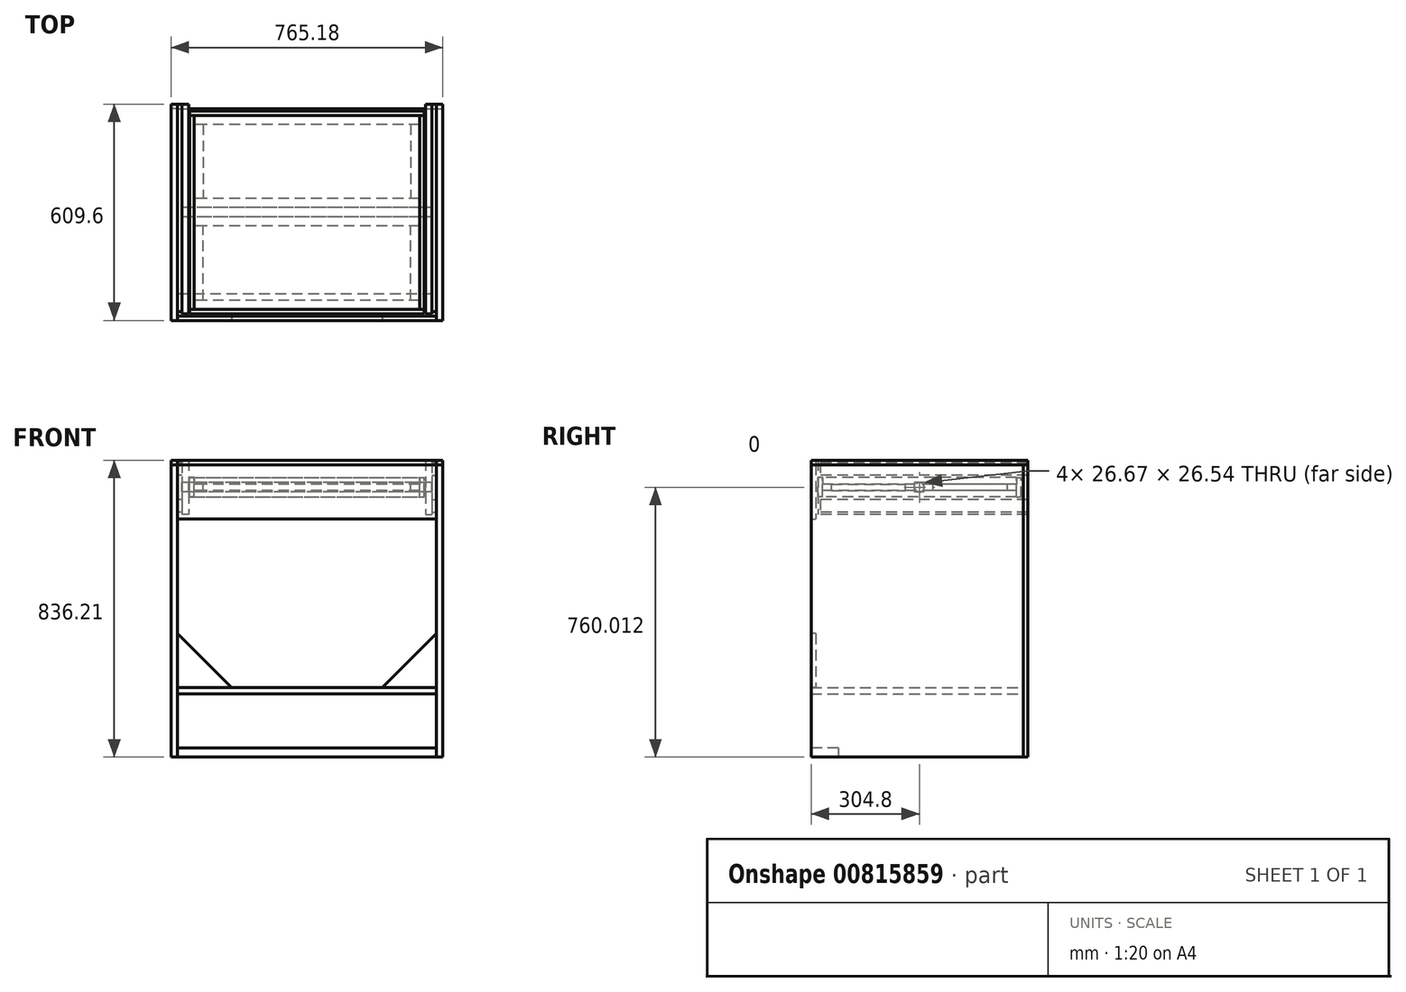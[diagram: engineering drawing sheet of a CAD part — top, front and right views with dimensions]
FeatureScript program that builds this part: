
annotation { "Feature Type Name" : "Feature", "Feature Type Description" : "" }
export const myFeature = defineFeature(function(context is Context, id is Id, definition is map)
    precondition{}
    {
        {
            var Q0;
            Q0=qCreatedBy(makeId("Top.planeOp"),FACE);
            var sketch = newSketch(context, id + "F0", { "sketchPlane" : qUnion([Q0])});
            skLineSegment(sketch, "E0.bottom", {"start": v(-317.5, 241.3) * mm, "end": v(317.5, 241.3) * mm});
            skLineSegment(sketch, "E0.top", {"start": v(-317.5, -304.8) * mm, "end": v(317.5, -304.8) * mm});
            skLineSegment(sketch, "E0.left", {"start": v(-317.5, 241.3) * mm, "end": v(-317.5, -304.8) * mm});
            skLineSegment(sketch, "E0.right", {"start": v(317.5, 241.3) * mm, "end": v(317.5, -304.8) * mm});
            skLineSegment(sketch, "E1", {"start": v(317.5, -18.41) * mm, "end": v(-317.5, -18.42) * mm});
            skLineSegment(sketch, "E2", {"start": v(317.5, -31.75) * mm, "end": v(-317.5, -31.75) * mm, "construction": true});
            skLineSegment(sketch, "E3", {"start": v(317.5, 6.99) * mm, "end": v(-317.5, 6.98) * mm});
            skLineSegment(sketch, "E4", {"start": v(317.5, 215.9) * mm, "end": v(-317.5, 215.9) * mm});
            skLineSegment(sketch, "E5", {"start": v(292.1, 215.9) * mm, "end": v(292.1, 6.98) * mm});
            skLineSegment(sketch, "E6", {"start": v(0, 0) * mm, "end": v(0, -123.63) * mm, "construction": true});
            skLineSegment(sketch, "E7.MirrorCS", {"start": v(-292.1, 215.9) * mm, "end": v(-292.1, 6.98) * mm});
            skLineSegment(sketch, "E8.MirrorCS", {"start": v(317.5, -45.08) * mm, "end": v(-317.5, -45.09) * mm});
            skLineSegment(sketch, "E9.MirrorCS", {"start": v(317.5, -70.48) * mm, "end": v(-317.5, -70.49) * mm});
            skLineSegment(sketch, "E10.MirrorCS", {"start": v(292.1, -279.4) * mm, "end": v(292.1, -70.49) * mm});
            skLineSegment(sketch, "E11.MirrorCS", {"start": v(317.5, -279.4) * mm, "end": v(-317.5, -279.4) * mm});
            skLineSegment(sketch, "E12.MirrorCS", {"start": v(-292.1, -279.4) * mm, "end": v(-292.1, -70.49) * mm});
            skSolve(sketch);
        }
        {
            var Q0;
            {var subQ1=sQuery(id+"F0.wireOp",EDGE,"E0.bottom");Q0=makeQuery(id+"F0.imprint","IMPRINT",FACE,{"disambiguationData":[TD([[makeQuery(id+"F0.imprint","IMPRINT",EDGE,{"derivedFrom":subQ1}),-1.0]])]});}
            var Q1;
            {var subQ0=sQuery(id+"F0.wireOp",EDGE,"E5");Q1=makeQuery(id+"F0.imprint","IMPRINT",FACE,{"disambiguationData":[TD([[makeQuery(id+"F0.imprint","IMPRINT",EDGE,{"derivedFrom":subQ0}),-1.0]])]});}
            var Q2;
            {var subQ5=sQuery(id+"F0.wireOp",EDGE,"E7.MirrorCS");Q2=makeQuery(id+"F0.imprint","IMPRINT",FACE,{"disambiguationData":[TD([[makeQuery(id+"F0.imprint","IMPRINT",EDGE,{"derivedFrom":subQ5}),-1.0]])]});}
            var Q3;
            {var subQ5=sQuery(id+"F0.wireOp",EDGE,"E5");Q3=makeQuery(id+"F0.imprint","IMPRINT",FACE,{"disambiguationData":[TD([[makeQuery(id+"F0.imprint","IMPRINT",EDGE,{"derivedFrom":subQ5}),1.0]])]});}
            var Q4;
            {var subQ4=sQuery(id+"F0.wireOp",EDGE,"E1");Q4=makeQuery(id+"F0.imprint","IMPRINT",FACE,{"disambiguationData":[TD([[makeQuery(id+"F0.imprint","IMPRINT",EDGE,{"derivedFrom":subQ4}),-1.0]])]});}
            var Q5;
            {var subQ0=sQuery(id+"F0.wireOp",EDGE,"E1");Q5=makeQuery(id+"F0.imprint","IMPRINT",FACE,{"disambiguationData":[TD([[makeQuery(id+"F0.imprint","IMPRINT",EDGE,{"derivedFrom":subQ0}),1.0]])]});}
            var Q6;
            {var subQ0=sQuery(id+"F0.wireOp",EDGE,"E8.MirrorCS");Q6=makeQuery(id+"F0.imprint","IMPRINT",FACE,{"disambiguationData":[TD([[makeQuery(id+"F0.imprint","IMPRINT",EDGE,{"derivedFrom":subQ0}),1.0]])]});}
            var Q7;
            {var subQ5=sQuery(id+"F0.wireOp",EDGE,"E10.MirrorCS");Q7=makeQuery(id+"F0.imprint","IMPRINT",FACE,{"disambiguationData":[TD([[makeQuery(id+"F0.imprint","IMPRINT",EDGE,{"derivedFrom":subQ5}),-1.0]])]});}
            var Q8;
            {var subQ0=sQuery(id+"F0.wireOp",EDGE,"E10.MirrorCS");Q8=makeQuery(id+"F0.imprint","IMPRINT",FACE,{"disambiguationData":[TD([[makeQuery(id+"F0.imprint","IMPRINT",EDGE,{"derivedFrom":subQ0}),1.0]])]});}
            var Q9;
            {var subQ5=sQuery(id+"F0.wireOp",EDGE,"E0.top");Q9=makeQuery(id+"F0.imprint","IMPRINT",FACE,{"disambiguationData":[TD([[makeQuery(id+"F0.imprint","IMPRINT",EDGE,{"derivedFrom":subQ5}),1.0]])]});}
            var Q10;
            {var subQ5=sQuery(id+"F0.wireOp",EDGE,"E12.MirrorCS");Q10=makeQuery(id+"F0.imprint","IMPRINT",FACE,{"disambiguationData":[TD([[makeQuery(id+"F0.imprint","IMPRINT",EDGE,{"derivedFrom":subQ5}),1.0]])]});}
            extrude(context, id + "F1", {"entities" : qUnion([Q0, Q1, Q2, Q3, Q4, Q5, Q6, Q7, Q8, Q9, Q10]), "depth" : 18.26 * mm, "offsetDistance" : 25.4 * mm});
        }
        {
            var Q0;
            {var subQ0=sQuery(id+"F0.wireOp",EDGE,"E1");Q0=makeQuery(id+"F0.imprint","IMPRINT",FACE,{"disambiguationData":[TD([[makeQuery(id+"F0.imprint","IMPRINT",EDGE,{"derivedFrom":subQ0}),1.0]])]});}
            extrude(context, id + "F2", {"entities" : qUnion([Q0]), "operationType" : NewBodyOperationType.REMOVE, "depth" : 4.14 * mm, "offsetDistance" : 25.4 * mm});
        }
        {
            var Q0;
            {var subQ0=sQuery(id+"F0.wireOp",EDGE,"E8.MirrorCS");Q0=makeQuery(id+"F0.imprint","IMPRINT",FACE,{"disambiguationData":[TD([[makeQuery(id+"F0.imprint","IMPRINT",EDGE,{"derivedFrom":subQ0}),1.0]])]});}
            var Q1;
            {var subQ4=sQuery(id+"F0.wireOp",EDGE,"E1");Q1=makeQuery(id+"F0.imprint","IMPRINT",FACE,{"disambiguationData":[TD([[makeQuery(id+"F0.imprint","IMPRINT",EDGE,{"derivedFrom":subQ4}),-1.0]])]});}
            var Q2;
            {var subQ1=sQuery(id+"F0.wireOp",EDGE,"E0.bottom");Q2=makeQuery(id+"F0.imprint","IMPRINT",FACE,{"disambiguationData":[TD([[makeQuery(id+"F0.imprint","IMPRINT",EDGE,{"derivedFrom":subQ1}),-1.0]])]});}
            var Q3;
            {var subQ5=sQuery(id+"F0.wireOp",EDGE,"E0.top");Q3=makeQuery(id+"F0.imprint","IMPRINT",FACE,{"disambiguationData":[TD([[makeQuery(id+"F0.imprint","IMPRINT",EDGE,{"derivedFrom":subQ5}),1.0]])]});}
            extrude(context, id + "F3", {"entities" : qUnion([Q0, Q1, Q2, Q3]), "oppositeDirection" : true, "depth" : 18.26 * mm, "offsetDistance" : 25.4 * mm});
        }
        {
            var Q0;
            {var subQ5=sQuery(id+"F0.wireOp",EDGE,"E10.MirrorCS");Q0=makeQuery(id+"F0.imprint","IMPRINT",FACE,{"disambiguationData":[TD([[makeQuery(id+"F0.imprint","IMPRINT",EDGE,{"derivedFrom":subQ5}),-1.0]])]});}
            var Q1;
            {var subQ5=sQuery(id+"F0.wireOp",EDGE,"E5");Q1=makeQuery(id+"F0.imprint","IMPRINT",FACE,{"disambiguationData":[TD([[makeQuery(id+"F0.imprint","IMPRINT",EDGE,{"derivedFrom":subQ5}),1.0]])]});}
            var Q2;
            {var subQ5=sQuery(id+"F0.wireOp",EDGE,"E7.MirrorCS");Q2=makeQuery(id+"F0.imprint","IMPRINT",FACE,{"disambiguationData":[TD([[makeQuery(id+"F0.imprint","IMPRINT",EDGE,{"derivedFrom":subQ5}),-1.0]])]});}
            var Q3;
            {var subQ5=sQuery(id+"F0.wireOp",EDGE,"E12.MirrorCS");Q3=makeQuery(id+"F0.imprint","IMPRINT",FACE,{"disambiguationData":[TD([[makeQuery(id+"F0.imprint","IMPRINT",EDGE,{"derivedFrom":subQ5}),1.0]])]});}
            extrude(context, id + "F4", {"entities" : qUnion([Q0, Q1, Q2, Q3]), "oppositeDirection" : true, "depth" : 18.26 * mm, "offsetDistance" : 25.4 * mm});
        }
        {
            var Q0;
            Q0=makeQuery(id+"F3.opExtrude","SWEPT_EDGE",EDGE,{"disambiguationData":[OSD([sQuery(id+"F0.wireOp",EDGE,"E0.top"),sQuery(id+"F0.wireOp",EDGE,"E0.left")])]});
            cPoint(context, id + "F5", {"entities" : qUnion([Q0]), "parameter" : 0.5});
        }
        {
            var Q0;
            Q0 = qCreatedBy(id + "F5" ,VERTEX);
            var Q1;
            Q1=makeQuery(id+"F3.opExtrude","SWEPT_EDGE",EDGE,{"disambiguationData":[OSD([sQuery(id+"F0.wireOp",EDGE,"E0.top"),sQuery(id+"F0.wireOp",EDGE,"E0.left")])]});
            cPlane(context, id + "F6", {"entities" : qUnion([Q0, Q1]), "cplaneType" : CPlaneType.CURVE_POINT, "offset" : 25.4 * mm, "width" : 152.4 * mm, "height" : 152.4 * mm});
        }
        {
            var Q0;
            Q0=makeQuery(id+"F1.opExtrude","SWEPT_BODY",BODY,{"disambiguationData":[OSD([sQuery(id+"F0.wireOp",EDGE,"E0.bottom"),sQuery(id+"F0.wireOp",EDGE,"E0.top"),sQuery(id+"F0.wireOp",EDGE,"E0.left"),sQuery(id+"F0.wireOp",EDGE,"E0.right")])]});
            var Q1;
            Q1=qCreatedBy(id+"F6.planeOp",FACE);
            mirror(context, id + "F7", {"entities" : qUnion([Q0]), "mirrorPlane" : qUnion([Q1])});
        }
        {
            var Q0;
            Q0=makeQuery(id+"F1.opExtrude","CAP_FACE",FACE,{"disambiguationData":[OSD([sQuery(id+"F0.wireOp",EDGE,"E0.bottom"),sQuery(id+"F0.wireOp",EDGE,"E0.top"),sQuery(id+"F0.wireOp",EDGE,"E0.left"),sQuery(id+"F0.wireOp",EDGE,"E0.right")])],"isStart":false});
            var sketch = newSketch(context, id + "F8", { "sketchPlane" : qUnion([Q0])});
            skLineSegment(sketch, "E13.bottom", {"start": v(-317.5, 241.3) * mm, "end": v(-330.2, 241.3) * mm});
            skLineSegment(sketch, "E13.top", {"start": v(-317.5, -304.8) * mm, "end": v(-330.2, -304.8) * mm});
            skLineSegment(sketch, "E13.left", {"start": v(-317.5, 241.3) * mm, "end": v(-317.5, -304.8) * mm});
            skLineSegment(sketch, "E13.right", {"start": v(-330.2, 241.3) * mm, "end": v(-330.2, -304.8) * mm});
            skLineSegment(sketch, "E14", {"start": v(0, 0) * mm, "end": v(0, 146.18) * mm, "construction": true});
            skLineSegment(sketch, "E15.MirrorCS", {"start": v(317.5, 241.3) * mm, "end": v(330.2, 241.3) * mm});
            skLineSegment(sketch, "E16.bottom", {"start": v(-330.2, 241.3) * mm, "end": v(330.2, 241.3) * mm});
            skLineSegment(sketch, "E16.top", {"start": v(-330.2, 254) * mm, "end": v(330.2, 254) * mm});
            skLineSegment(sketch, "E16.left", {"start": v(-330.2, 241.3) * mm, "end": v(-330.2, 254) * mm});
            skLineSegment(sketch, "E16.right", {"start": v(330.2, 241.3) * mm, "end": v(330.2, 254) * mm});
            skLineSegment(sketch, "E17.MirrorCS", {"start": v(317.5, 241.3) * mm, "end": v(317.5, -304.8) * mm});
            skLineSegment(sketch, "E18.MirrorCS", {"start": v(330.2, 241.3) * mm, "end": v(330.2, -304.8) * mm});
            skLineSegment(sketch, "E19.MirrorCS", {"start": v(317.5, -304.8) * mm, "end": v(330.2, -304.8) * mm});
            skLineSegment(sketch, "E20", {"start": v(317.5, -31.75) * mm, "end": v(-151.21, -31.75) * mm, "construction": true});
            skLineSegment(sketch, "E21.MirrorCS", {"start": v(-330.2, -304.8) * mm, "end": v(330.2, -304.8) * mm});
            skLineSegment(sketch, "E22.MirrorCS", {"start": v(-330.2, -317.5) * mm, "end": v(330.2, -317.5) * mm});
            skLineSegment(sketch, "E23.MirrorCS", {"start": v(330.2, -304.8) * mm, "end": v(330.2, -317.5) * mm});
            skLineSegment(sketch, "E24.MirrorCS", {"start": v(-330.2, -304.8) * mm, "end": v(-330.2, -317.5) * mm});
            skSolve(sketch);
        }
        {
            var Q0;
            Q0=makeQuery(id+"F8.imprint","IMPRINT",FACE,{"disambiguationData":[TD([[makeQuery(id+"F8.imprint","IMPRINT",EDGE,{"derivedFrom":sQuery(id+"F8.wireOp",EDGE,"E22.MirrorCS")}),1.0]])]});
            var Q1;
            Q1=makeQuery(id+"F8.imprint","IMPRINT",FACE,{"disambiguationData":[TD([[makeQuery(id+"F8.imprint","IMPRINT",EDGE,{"derivedFrom":sQuery(id+"F8.wireOp",EDGE,"E16.top")}),-1.0]])]});
            var Q2;
            Q2=makeQuery(id+"F7.opPattern","COPY",FACE,{"derivedFrom":makeQuery(id+"F1.opExtrude","CAP_FACE",FACE,{"disambiguationData":[OSD([sQuery(id+"F0.wireOp",EDGE,"E0.bottom"),sQuery(id+"F0.wireOp",EDGE,"E0.top"),sQuery(id+"F0.wireOp",EDGE,"E0.left"),sQuery(id+"F0.wireOp",EDGE,"E0.right")])],"isStart":false}),"instanceName":"1"});
            extrude(context, id + "F9", {"entities" : qUnion([Q0, Q1]), "endBound" : BoundingType.UP_TO_SURFACE, "oppositeDirection" : true, "depth" : 25.4 * mm, "endBoundEntityFace" : qUnion([Q2]), "offsetDistance" : 25.4 * mm});
        }
        {
            var Q0;
            {var subQ0=sQuery(id+"F8.wireOp",EDGE,"E17.MirrorCS");Q0=makeQuery(id+"F8.imprint","IMPRINT",FACE,{"disambiguationData":[TD([[makeQuery(id+"F8.imprint","IMPRINT",EDGE,{"derivedFrom":subQ0}),1.0]])]});}
            var Q1;
            {var subQ0=sQuery(id+"F8.wireOp",EDGE,"E13.left");Q1=makeQuery(id+"F8.imprint","IMPRINT",FACE,{"disambiguationData":[TD([[makeQuery(id+"F8.imprint","IMPRINT",EDGE,{"derivedFrom":subQ0}),-1.0]])]});}
            var Q2;
            Q2=makeQuery(id+"F7.opPattern","COPY",FACE,{"derivedFrom":makeQuery(id+"F1.opExtrude","CAP_FACE",FACE,{"disambiguationData":[OSD([sQuery(id+"F0.wireOp",EDGE,"E0.bottom"),sQuery(id+"F0.wireOp",EDGE,"E0.top"),sQuery(id+"F0.wireOp",EDGE,"E0.left"),sQuery(id+"F0.wireOp",EDGE,"E0.right")])],"isStart":false}),"instanceName":"1"});
            extrude(context, id + "F10", {"entities" : qUnion([Q0, Q1]), "endBound" : BoundingType.UP_TO_SURFACE, "oppositeDirection" : true, "depth" : 25.4 * mm, "endBoundEntityFace" : qUnion([Q2]), "offsetDistance" : 25.4 * mm});
        }
        {
            var Q0;
            Q0=makeQuery(id+"F10.opExtrude","SWEPT_FACE",FACE,{"disambiguationData":[OSD([sQuery(id+"F8.wireOp",EDGE,"E13.right")])]});
            var sketch = newSketch(context, id + "F11", { "sketchPlane" : qUnion([Q0])});
            skLineSegment(sketch, "E25.0", {"start": v(18.41, -22.4) * mm, "end": v(45.08, -22.4) * mm});
            skLineSegment(sketch, "E26.0", {"start": v(45.08, -22.4) * mm, "end": v(45.08, -18.26) * mm});
            skLineSegment(sketch, "E27.0", {"start": v(45.08, -18.26) * mm, "end": v(45.08, 0) * mm});
            skLineSegment(sketch, "E28.0", {"start": v(18.41, -22.4) * mm, "end": v(18.41, -18.26) * mm});
            skLineSegment(sketch, "E29.0", {"start": v(18.41, -18.26) * mm, "end": v(18.41, 0) * mm});
            skLineSegment(sketch, "E30.0", {"start": v(45.08, 4.14) * mm, "end": v(45.08, 0) * mm});
            skLineSegment(sketch, "E31.0", {"start": v(18.41, 4.14) * mm, "end": v(45.08, 4.14) * mm});
            skLineSegment(sketch, "E32.0", {"start": v(18.41, 4.14) * mm, "end": v(18.41, 0) * mm});
            skSolve(sketch);
        }
        {
            var Q0;
            Q0=makeQuery(id+"F11.imprint","IMPRINT",FACE,{"disambiguationData":[TD([[makeQuery(id+"F11.imprint","IMPRINT",EDGE,{"derivedFrom":sQuery(id+"F11.wireOp",EDGE,"E25.0")}),1.0]])]});
            extrude(context, id + "F12", {"entities" : qUnion([Q0]), "operationType" : NewBodyOperationType.REMOVE, "endBound" : BoundingType.THROUGH_ALL, "oppositeDirection" : true, "depth" : 697.23 * mm, "offsetDistance" : 25.4 * mm});
        }
        {
            var Q0;
            Q0=makeQuery(id+"F10.opExtrude","CAP_EDGE",EDGE,{"disambiguationData":[OSD([sQuery(id+"F8.wireOp",EDGE,"E13.right")])],"isStart":true});
            cPoint(context, id + "F13", {"entities" : qUnion([Q0]), "parameter" : 0.5});
        }
        {
            var Q0;
            Q0=makeQuery(id+"F10.opExtrude","CAP_EDGE",EDGE,{"disambiguationData":[OSD([sQuery(id+"F8.wireOp",EDGE,"E13.right")])],"isStart":true});
            var Q1;
            Q1 = qCreatedBy(id + "F13" ,VERTEX);
            cPlane(context, id + "F14", {"entities" : qUnion([Q0, Q1]), "cplaneType" : CPlaneType.CURVE_POINT, "offset" : 25.4 * mm, "width" : 152.4 * mm, "height" : 152.4 * mm});
        }
        {
            var Q0;
            Q0=qCreatedBy(id+"F14.planeOp",FACE);
            var sketch = newSketch(context, id + "F15", { "sketchPlane" : qUnion([Q0])});
            skLineSegment(sketch, "E33", {"start": v(0, 0) * mm, "end": v(0, 132.1) * mm, "construction": true});
            skLineSegment(sketch, "E34.bottom", {"start": v(-333.38, 67.07) * mm, "end": v(-351.63, 67.07) * mm});
            skLineSegment(sketch, "E34.top", {"start": v(-333.38, -85.33) * mm, "end": v(-351.63, -85.33) * mm});
            skLineSegment(sketch, "E34.left", {"start": v(-333.38, 67.07) * mm, "end": v(-333.38, -85.33) * mm});
            skLineSegment(sketch, "E34.right", {"start": v(-351.63, 67.07) * mm, "end": v(-351.63, -85.33) * mm});
            skLineSegment(sketch, "E35", {"start": v(341.33, -9.13) * mm, "end": v(-243, -9.13) * mm, "construction": true});
            skLineSegment(sketch, "E36.MirrorCS", {"start": v(333.38, 67.07) * mm, "end": v(351.63, 67.07) * mm});
            skLineSegment(sketch, "E37.MirrorCS", {"start": v(333.38, 67.07) * mm, "end": v(333.38, -85.33) * mm});
            skLineSegment(sketch, "E38.MirrorCS", {"start": v(351.63, 67.07) * mm, "end": v(351.63, -85.33) * mm});
            skLineSegment(sketch, "E39.MirrorCS", {"start": v(333.38, -85.33) * mm, "end": v(351.63, -85.33) * mm});
            skLineSegment(sketch, "E40.bottom", {"start": v(-351.63, 60.72) * mm, "end": v(-364.33, 60.72) * mm});
            skLineSegment(sketch, "E40.top", {"start": v(-351.63, 25.16) * mm, "end": v(-364.33, 25.16) * mm});
            skLineSegment(sketch, "E40.left", {"start": v(-351.63, 60.72) * mm, "end": v(-351.63, 25.16) * mm});
            skLineSegment(sketch, "E40.right", {"start": v(-364.33, 60.72) * mm, "end": v(-364.33, 25.16) * mm});
            skLineSegment(sketch, "E41.MirrorCS", {"start": v(-351.63, -78.98) * mm, "end": v(-364.33, -78.98) * mm});
            skLineSegment(sketch, "E42.MirrorCS", {"start": v(-364.33, -78.98) * mm, "end": v(-364.33, -43.42) * mm});
            skLineSegment(sketch, "E43.MirrorCS", {"start": v(-351.63, -43.42) * mm, "end": v(-364.33, -43.42) * mm});
            skLineSegment(sketch, "E44.MirrorCS", {"start": v(351.63, 60.72) * mm, "end": v(364.33, 60.72) * mm});
            skLineSegment(sketch, "E45.MirrorCS", {"start": v(364.33, 60.72) * mm, "end": v(364.33, 25.16) * mm});
            skLineSegment(sketch, "E46.MirrorCS", {"start": v(351.63, 25.16) * mm, "end": v(364.33, 25.16) * mm});
            skLineSegment(sketch, "E47.MirrorCS", {"start": v(351.63, -43.42) * mm, "end": v(364.33, -43.42) * mm});
            skLineSegment(sketch, "E48.MirrorCS", {"start": v(364.33, -78.98) * mm, "end": v(364.33, -43.42) * mm});
            skLineSegment(sketch, "E49.MirrorCS", {"start": v(351.63, -78.98) * mm, "end": v(364.33, -78.98) * mm});
            skLineSegment(sketch, "E50.0", {"start": v(-330.2, -36.51) * mm, "end": v(-330.2, 18.26) * mm, "construction": true});
            skSolve(sketch);
        }
        {
            var Q0;
            {var subQ1=sQuery(id+"F15.wireOp",EDGE,"E34.bottom");Q0=makeQuery(id+"F15.imprint","IMPRINT",FACE,{"disambiguationData":[TD([[makeQuery(id+"F15.imprint","IMPRINT",EDGE,{"derivedFrom":subQ1}),1.0]])]});}
            var Q1;
            {var subQ3=sQuery(id+"F15.wireOp",EDGE,"E36.MirrorCS");Q1=makeQuery(id+"F15.imprint","IMPRINT",FACE,{"disambiguationData":[TD([[makeQuery(id+"F15.imprint","IMPRINT",EDGE,{"derivedFrom":subQ3}),-1.0]])]});}
            extrude(context, id + "F16", {"entities" : qUnion([Q0, Q1]), "oppositeDirection" : true, "depth" : 304.8 * mm, "offsetDistance" : 25.4 * mm, "hasSecondDirection" : true, "secondDirectionOppositeDirection" : false, "secondDirectionDepth" : 285.75 * mm});
        }
        {
            var Q0;
            Q0=makeQuery(id+"F15.imprint","IMPRINT",FACE,{"disambiguationData":[TD([[makeQuery(id+"F15.imprint","IMPRINT",EDGE,{"derivedFrom":sQuery(id+"F15.wireOp",EDGE,"E40.bottom")}),1.0]])]});
            var Q1;
            {var subQ0=sQuery(id+"F15.wireOp",EDGE,"E41.MirrorCS");Q1=makeQuery(id+"F15.imprint","IMPRINT",FACE,{"disambiguationData":[TD([[makeQuery(id+"F15.imprint","IMPRINT",EDGE,{"derivedFrom":subQ0}),-1.0]])]});}
            var Q2;
            {var subQ0=sQuery(id+"F15.wireOp",EDGE,"E44.MirrorCS");Q2=makeQuery(id+"F15.imprint","IMPRINT",FACE,{"disambiguationData":[TD([[makeQuery(id+"F15.imprint","IMPRINT",EDGE,{"derivedFrom":subQ0}),-1.0]])]});}
            var Q3;
            {var subQ0=sQuery(id+"F15.wireOp",EDGE,"E47.MirrorCS");Q3=makeQuery(id+"F15.imprint","IMPRINT",FACE,{"disambiguationData":[TD([[makeQuery(id+"F15.imprint","IMPRINT",EDGE,{"derivedFrom":subQ0}),-1.0]])]});}
            extrude(context, id + "F17", {"entities" : qUnion([Q0, Q1, Q2, Q3]), "oppositeDirection" : true, "depth" : 304.8 * mm, "offsetDistance" : 25.4 * mm, "hasSecondDirection" : true, "secondDirectionOppositeDirection" : false, "secondDirectionDepth" : 279.4 * mm});
        }
        {
            var Q0;
            Q0 = qSketchRegion(id + "F11", true);
            extrude(context, id + "F18", {"entities" : qUnion([Q0]), "operationType" : NewBodyOperationType.REMOVE, "endBound" : BoundingType.THROUGH_ALL, "oppositeDirection" : true, "depth" : 25.4 * mm, "offsetDistance" : 25.4 * mm, "hasSecondDirection" : true, "secondDirectionBound" : SecondDirectionBoundingType.THROUGH_ALL, "secondDirectionOppositeDirection" : false, "secondDirectionDepth" : 25.4 * mm});
        }
        {
            var Q0;
            Q0=qCreatedBy(id+"F14.planeOp",FACE);
            var sketch = newSketch(context, id + "F19", { "sketchPlane" : qUnion([Q0])});
            skLineSegment(sketch, "E51.0", {"start": v(-351.63, 67.07) * mm, "end": v(-333.38, 67.07) * mm, "construction": true});
            skLineSegment(sketch, "E52.0", {"start": v(-364.33, 25.16) * mm, "end": v(-364.33, 60.72) * mm, "construction": true});
            skLineSegment(sketch, "E53.bottom", {"start": v(-364.33, 67.07) * mm, "end": v(-382.59, 67.07) * mm});
            skLineSegment(sketch, "E53.top", {"start": v(-364.33, -769.14) * mm, "end": v(-382.59, -769.14) * mm});
            skLineSegment(sketch, "E53.left", {"start": v(-364.33, 67.07) * mm, "end": v(-364.33, -769.14) * mm});
            skLineSegment(sketch, "E53.right", {"start": v(-382.59, 67.07) * mm, "end": v(-382.59, -769.14) * mm});
            skLineSegment(sketch, "E54", {"start": v(0, 0) * mm, "end": v(0, -185.66) * mm, "construction": true});
            skLineSegment(sketch, "E55.MirrorCS", {"start": v(364.33, 67.07) * mm, "end": v(364.33, -769.14) * mm});
            skLineSegment(sketch, "E56.MirrorCS", {"start": v(382.59, 67.07) * mm, "end": v(382.59, -769.14) * mm});
            skLineSegment(sketch, "E57.MirrorCS", {"start": v(364.33, -769.14) * mm, "end": v(382.59, -769.14) * mm});
            skLineSegment(sketch, "E58.MirrorCS", {"start": v(364.33, 67.07) * mm, "end": v(382.59, 67.07) * mm});
            skLineSegment(sketch, "E59.0", {"start": v(-364.33, 54.37) * mm, "end": v(-382.59, 54.37) * mm});
            skLineSegment(sketch, "E60.MirrorCS", {"start": v(364.33, 54.37) * mm, "end": v(382.59, 54.37) * mm});
            skSolve(sketch);
        }
        {
            var Q0;
            {var subQ0=sQuery(id+"F19.wireOp",EDGE,"E53.bottom");Q0=makeQuery(id+"F19.imprint","IMPRINT",FACE,{"disambiguationData":[TD([[makeQuery(id+"F19.imprint","IMPRINT",EDGE,{"derivedFrom":subQ0}),1.0]])]});}
            var Q1;
            {var subQ0=sQuery(id+"F19.wireOp",EDGE,"E58.MirrorCS");Q1=makeQuery(id+"F19.imprint","IMPRINT",FACE,{"disambiguationData":[TD([[makeQuery(id+"F19.imprint","IMPRINT",EDGE,{"derivedFrom":subQ0}),-1.0]])]});}
            extrude(context, id + "F20", {"entities" : qUnion([Q0, Q1]), "endBound" : BoundingType.SYMMETRIC, "depth" : 609.6 * mm, "offsetDistance" : 25.4 * mm});
        }
        {
            var Q0;
            {var subQ0=sQuery(id+"F19.wireOp",EDGE,"E53.top");Q0=makeQuery(id+"F19.imprint","IMPRINT",FACE,{"disambiguationData":[TD([[makeQuery(id+"F19.imprint","IMPRINT",EDGE,{"derivedFrom":subQ0}),-1.0]])]});}
            var Q1;
            {var subQ0=sQuery(id+"F19.wireOp",EDGE,"E57.MirrorCS");Q1=makeQuery(id+"F19.imprint","IMPRINT",FACE,{"disambiguationData":[TD([[makeQuery(id+"F19.imprint","IMPRINT",EDGE,{"derivedFrom":subQ0}),1.0]])]});}
            extrude(context, id + "F21", {"entities" : qUnion([Q0, Q1]), "depth" : 304.8 * mm, "offsetDistance" : 25.4 * mm, "hasSecondDirection" : true, "secondDirectionOppositeDirection" : true, "secondDirectionDepth" : 292.1 * mm});
        }
        {
            var Q0;
            Q0=makeQuery(id+"F20.opExtrude","SWEPT_FACE",FACE,{"disambiguationData":[OSD([sQuery(id+"F19.wireOp",EDGE,"E59.0")])]});
            var sketch = newSketch(context, id + "F22", { "sketchPlane" : qUnion([Q0])});
            skLineSegment(sketch, "E61.0", {"start": v(-364.33, 336.55) * mm, "end": v(-382.59, 336.55) * mm});
            skLineSegment(sketch, "E62.0", {"start": v(-382.59, 336.55) * mm, "end": v(-382.59, -273.05) * mm});
            skLineSegment(sketch, "E63.0", {"start": v(-364.33, 336.55) * mm, "end": v(-364.33, -273.05) * mm});
            skLineSegment(sketch, "E64.0", {"start": v(-364.33, -273.05) * mm, "end": v(-382.59, -273.05) * mm});
            skLineSegment(sketch, "E65.0", {"start": v(-364.33, -260.35) * mm, "end": v(-382.59, -260.35) * mm});
            skLineSegment(sketch, "E66.0", {"start": v(364.33, -260.35) * mm, "end": v(382.59, -260.35) * mm});
            skLineSegment(sketch, "E67.0", {"start": v(364.33, 336.55) * mm, "end": v(364.33, -273.05) * mm});
            skLineSegment(sketch, "E68.0", {"start": v(364.33, -273.05) * mm, "end": v(382.59, -273.05) * mm});
            skLineSegment(sketch, "E69.0", {"start": v(382.59, 336.55) * mm, "end": v(382.59, -273.05) * mm});
            skLineSegment(sketch, "E70.0", {"start": v(364.33, 336.55) * mm, "end": v(382.59, 336.55) * mm});
            skSolve(sketch);
        }
        {
            var Q0;
            {var subQ0=sQuery(id+"F22.wireOp",EDGE,"E64.0");Q0=makeQuery(id+"F22.imprint","IMPRINT",FACE,{"disambiguationData":[TD([[makeQuery(id+"F22.imprint","IMPRINT",EDGE,{"derivedFrom":subQ0}),-1.0]])]});}
            var Q1;
            {var subQ0=sQuery(id+"F22.wireOp",EDGE,"E66.0");Q1=makeQuery(id+"F22.imprint","IMPRINT",FACE,{"disambiguationData":[TD([[makeQuery(id+"F22.imprint","IMPRINT",EDGE,{"derivedFrom":subQ0}),-1.0]])]});}
            var Q2;
            Q2=makeQuery(id+"F21.opExtrude","SWEPT_FACE",FACE,{"disambiguationData":[OSD([sQuery(id+"F19.wireOp",EDGE,"E57.MirrorCS")])]});
            extrude(context, id + "F23", {"entities" : qUnion([Q0, Q1]), "endBound" : BoundingType.UP_TO_SURFACE, "depth" : 25.4 * mm, "endBoundEntityFace" : qUnion([Q2]), "offsetDistance" : 25.4 * mm});
        }
        {
            var Q0;
            Q0=makeQuery(id+"F21.opExtrude","SWEPT_FACE",FACE,{"disambiguationData":[OSD([sQuery(id+"F19.wireOp",EDGE,"E55.MirrorCS")])]});
            var sketch = newSketch(context, id + "F24", { "sketchPlane" : qUnion([Q0])});
            skLineSegment(sketch, "E71.0", {"start": v(-260.35, -769.14) * mm, "end": v(-260.35, 54.37) * mm, "construction": true});
            skLineSegment(sketch, "E72", {"start": v(38.1, -769.14) * mm, "end": v(38.1, -684.42) * mm, "construction": true});
            skLineSegment(sketch, "E73.bottom", {"start": v(-184.15, -769.14) * mm, "end": v(-260.35, -769.14) * mm});
            skLineSegment(sketch, "E73.top", {"start": v(-184.15, -743.74) * mm, "end": v(-260.35, -743.74) * mm});
            skLineSegment(sketch, "E73.left", {"start": v(-260.35, -769.14) * mm, "end": v(-260.35, -743.74) * mm});
            skLineSegment(sketch, "E73.right", {"start": v(-184.15, -769.14) * mm, "end": v(-184.15, -743.74) * mm});
            skLineSegment(sketch, "E74.bottom", {"start": v(-260.35, -769.14) * mm, "end": v(-184.15, -769.14) * mm});
            skLineSegment(sketch, "E74.top", {"start": v(-260.35, -743.74) * mm, "end": v(-184.15, -743.74) * mm});
            skLineSegment(sketch, "E75.bottom", {"start": v(-260.35, -591.34) * mm, "end": v(-260.35, -591.34) * mm});
            skLineSegment(sketch, "E76.bottom", {"start": v(336.55, -769.14) * mm, "end": v(260.35, -769.14) * mm});
            skLineSegment(sketch, "E76.top", {"start": v(336.55, -743.74) * mm, "end": v(260.35, -743.74) * mm});
            skLineSegment(sketch, "E76.left", {"start": v(336.55, -769.14) * mm, "end": v(336.55, -743.74) * mm});
            skLineSegment(sketch, "E76.right", {"start": v(260.35, -769.14) * mm, "end": v(260.35, -743.74) * mm});
            skLineSegment(sketch, "E77.bottom", {"start": v(-260.35, -591.34) * mm, "end": v(336.55, -591.34) * mm});
            skLineSegment(sketch, "E77.top", {"start": v(-260.35, -573.65) * mm, "end": v(336.55, -573.65) * mm});
            skLineSegment(sketch, "E77.left", {"start": v(-260.35, -591.34) * mm, "end": v(-260.35, -573.65) * mm});
            skLineSegment(sketch, "E77.right", {"start": v(336.55, -591.34) * mm, "end": v(336.55, -573.65) * mm});
            skSolve(sketch);
        }
        {
            var Q0;
            Q0=makeQuery(id+"F24.imprint","IMPRINT",FACE,{"disambiguationData":[TD([[makeQuery(id+"F24.imprint","IMPRINT",EDGE,{"derivedFrom":sQuery(id+"F24.wireOp",EDGE,"E74.bottom")}),-1.0]])]});
            var Q1;
            Q1=makeQuery(id+"F24.imprint","IMPRINT",FACE,{"disambiguationData":[TD([[makeQuery(id+"F24.imprint","IMPRINT",EDGE,{"derivedFrom":sQuery(id+"F24.wireOp",EDGE,"E76.bottom")}),-1.0]])]});
            var Q2;
            Q2=makeQuery(id+"F24.imprint","IMPRINT",FACE,{"disambiguationData":[TD([[makeQuery(id+"F24.imprint","IMPRINT",EDGE,{"derivedFrom":sQuery(id+"F24.wireOp",EDGE,"E77.bottom")}),1.0]])]});
            var Q3;
            Q3=makeQuery(id+"F21.opExtrude","SWEPT_FACE",FACE,{"disambiguationData":[OSD([sQuery(id+"F19.wireOp",EDGE,"E53.left")])]});
            extrude(context, id + "F25", {"entities" : qUnion([Q0, Q1, Q2]), "endBound" : BoundingType.UP_TO_SURFACE, "depth" : 25.4 * mm, "endBoundEntityFace" : qUnion([Q3]), "offsetDistance" : 25.4 * mm});
        }
        {
            var Q0;
            Q0=makeQuery(id+"F21.opExtrude","SWEPT_FACE",FACE,{"disambiguationData":[OSD([sQuery(id+"F19.wireOp",EDGE,"E53.left")])]});
            var sketch = newSketch(context, id + "F26", { "sketchPlane" : qUnion([Q0])});
            skLineSegment(sketch, "E78.bottom", {"start": v(-336.55, 54.37) * mm, "end": v(-323.85, 54.37) * mm});
            skLineSegment(sketch, "E78.top", {"start": v(-336.55, -98.03) * mm, "end": v(-323.85, -98.03) * mm});
            skLineSegment(sketch, "E78.left", {"start": v(-336.55, 54.37) * mm, "end": v(-336.55, -98.03) * mm});
            skLineSegment(sketch, "E78.right", {"start": v(-323.85, 54.37) * mm, "end": v(-323.85, -98.03) * mm});
            skLineSegment(sketch, "E79.0", {"start": v(-336.55, 67.07) * mm, "end": v(-336.55, 54.37) * mm});
            skLineSegment(sketch, "E80", {"start": v(-336.55, 67.07) * mm, "end": v(-323.85, 67.07) * mm});
            skLineSegment(sketch, "E81", {"start": v(-323.85, 67.07) * mm, "end": v(-323.85, 54.37) * mm});
            skSolve(sketch);
        }
        {
            var Q0;
            Q0=makeQuery(id+"F26.imprint","IMPRINT",FACE,{"disambiguationData":[TD([[makeQuery(id+"F26.imprint","IMPRINT",EDGE,{"derivedFrom":sQuery(id+"F26.wireOp",EDGE,"E78.bottom")}),-1.0]])]});
            extrude(context, id + "F27", {"entities" : qUnion([Q0]), "endBound" : BoundingType.UP_TO_NEXT, "depth" : 25.4 * mm, "offsetDistance" : 25.4 * mm});
        }
        {
            var Q0;
            Q0=makeQuery(id+"F26.imprint","IMPRINT",FACE,{"disambiguationData":[TD([[makeQuery(id+"F26.imprint","IMPRINT",EDGE,{"derivedFrom":sQuery(id+"F26.wireOp",EDGE,"E78.bottom")}),1.0]])]});
            extrude(context, id + "F28", {"entities" : qUnion([Q0]), "endBound" : BoundingType.UP_TO_NEXT, "depth" : 25.4 * mm, "offsetDistance" : 25.4 * mm});
        }
        {
            var Q0;
            Q0=makeQuery(id+"F21.opExtrude","CAP_FACE",FACE,{"disambiguationData":[OSD([sQuery(id+"F19.wireOp",EDGE,"E53.top"),sQuery(id+"F19.wireOp",EDGE,"E53.left"),sQuery(id+"F19.wireOp",EDGE,"E53.right"),sQuery(id+"F19.wireOp",EDGE,"E59.0")])],"isStart":false});
            var sketch = newSketch(context, id + "F29", { "sketchPlane" : qUnion([Q0])});
            skLineSegment(sketch, "E82.0", {"start": v(-364.33, -573.65) * mm, "end": v(364.33, -573.65) * mm, "construction": true});
            skLineSegment(sketch, "E83.bottom", {"start": v(-364.33, -573.65) * mm, "end": v(-211.93, -573.65) * mm});
            skLineSegment(sketch, "E83.left", {"start": v(-364.33, -573.65) * mm, "end": v(-364.33, -421.25) * mm});
            skLineSegment(sketch, "E84", {"start": v(0, -573.65) * mm, "end": v(0, -484.6) * mm, "construction": true});
            skLineSegment(sketch, "E85", {"start": v(-364.33, -421.25) * mm, "end": v(-211.93, -573.65) * mm});
            skLineSegment(sketch, "E86.MirrorCS", {"start": v(364.33, -573.65) * mm, "end": v(364.33, -421.25) * mm});
            skLineSegment(sketch, "E87.MirrorCS", {"start": v(364.33, -573.65) * mm, "end": v(211.93, -573.65) * mm});
            skLineSegment(sketch, "E88.MirrorCS", {"start": v(364.33, -421.25) * mm, "end": v(211.93, -573.65) * mm});
            skSolve(sketch);
        }
        {
            var Q0;
            Q0=makeQuery(id+"F29.imprint","IMPRINT",FACE,{"disambiguationData":[TD([[makeQuery(id+"F29.imprint","IMPRINT",EDGE,{"derivedFrom":sQuery(id+"F29.wireOp",EDGE,"E83.bottom")}),1.0]])]});
            var Q1;
            Q1=makeQuery(id+"F29.imprint","IMPRINT",FACE,{"disambiguationData":[TD([[makeQuery(id+"F29.imprint","IMPRINT",EDGE,{"derivedFrom":sQuery(id+"F29.wireOp",EDGE,"E86.MirrorCS")}),1.0]])]});
            extrude(context, id + "F30", {"entities" : qUnion([Q0, Q1]), "oppositeDirection" : true, "depth" : 12.7 * mm, "offsetDistance" : 25.4 * mm});
        }
        {
            var Q0;
            Q0=makeQuery(id+"F16.opExtrude","SWEPT_FACE",FACE,{"disambiguationData":[OSD([sQuery(id+"F15.wireOp",EDGE,"E34.right"),sQuery(id+"F15.wireOp",EDGE,"E40.left")])]});
            var sketch = newSketch(context, id + "F31", { "sketchPlane" : qUnion([Q0])});
            skLineSegment(sketch, "E89", {"start": v(18.41, 4.14) * mm, "end": v(45.08, -22.4) * mm, "construction": true});
            skCircle(sketch, "E90", {"center": v(31.75, -9.13) * mm, "radius": 13.27 * mm});
            skSolve(sketch);
        }
        {
            var Q0;
            {var subQ0=sQuery(id+"F31.wireOp",EDGE,"E90");var subQ1=makeQuery(id+"F16.opExtrude","SWEPT_FACE",FACE,{"disambiguationData":[OSD([sQuery(id+"F15.wireOp",EDGE,"E34.right"),sQuery(id+"F15.wireOp",EDGE,"E40.left")])]});var subQ2=makeQuery(id+"F31.imprint","INTERSECT",VERTEX,{"derivedFrom":[makeQuery(id+"F18.boolean.opBoolean","INTERSECT",EDGE,{"derivedFrom":[subQ1,makeQuery(id+"F18.opExtrude","SWEPT_FACE",FACE,{"disambiguationData":[OSD([sQuery(id+"F11.wireOp",EDGE,"E25.0")])]})]}),subQ0]});Q0=makeQuery(id+"F31.imprint","IMPRINT",FACE,{"disambiguationData":[TD([[makeQuery(id+"F31.imprint","IMPRINT",EDGE,{"disambiguationData":[TD([[subQ2,1.0]])],"derivedFrom":subQ0}),1.0]])]});}
            var Q1;
            Q1=makeQuery(id+"F16.opExtrude","SWEPT_FACE",FACE,{"disambiguationData":[OSD([sQuery(id+"F15.wireOp",EDGE,"E38.MirrorCS")])]});
            extrude(context, id + "F32", {"entities" : qUnion([Q0]), "endBound" : BoundingType.UP_TO_SURFACE, "oppositeDirection" : true, "depth" : 25.4 * mm, "endBoundEntityFace" : qUnion([Q1]), "offsetDistance" : 25.4 * mm});
        }
    });
